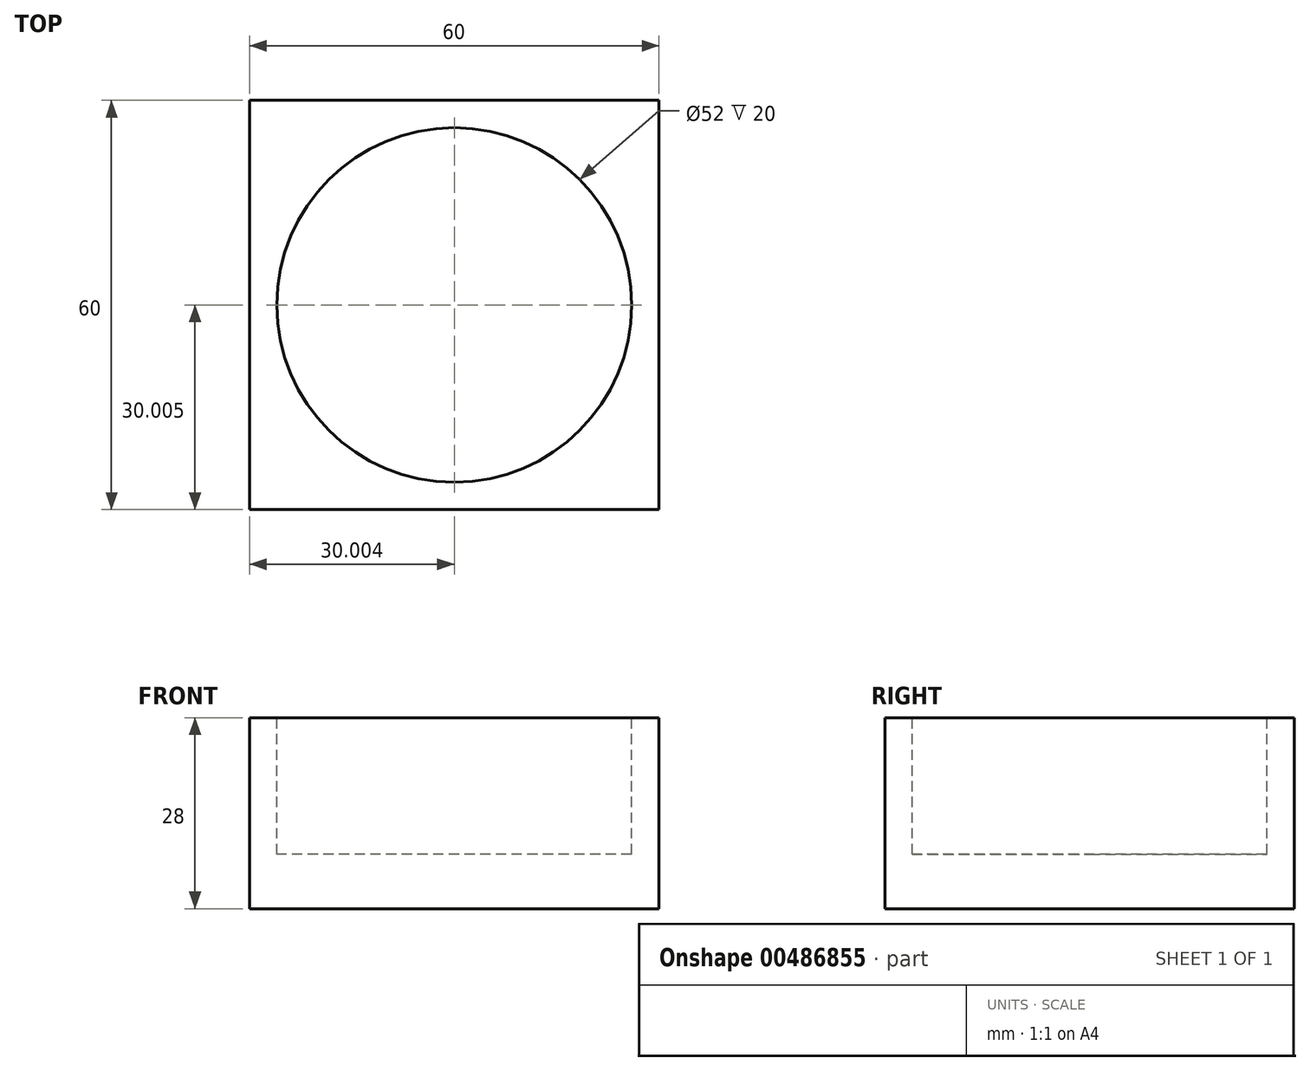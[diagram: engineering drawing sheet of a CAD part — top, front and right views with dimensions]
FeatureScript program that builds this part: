
annotation { "Feature Type Name" : "Feature", "Feature Type Description" : "" }
export const myFeature = defineFeature(function(context is Context, id is Id, definition is map)
    precondition{}
    {
        {
            var Q0;
            Q0=qCreatedBy(makeId("Top.planeOp"),FACE);
            var sketch = newSketch(context, id + "F0", { "sketchPlane" : qUnion([Q0])});
            skLineSegment(sketch, "E0.bottom", {"start": v(-12.17, 33.3) * mm, "end": v(47.83, 33.3) * mm});
            skLineSegment(sketch, "E0.top", {"start": v(-12.17, -26.7) * mm, "end": v(47.83, -26.7) * mm});
            skLineSegment(sketch, "E0.left", {"start": v(-12.17, 33.3) * mm, "end": v(-12.17, -26.7) * mm});
            skLineSegment(sketch, "E0.right", {"start": v(47.83, 33.3) * mm, "end": v(47.83, -26.7) * mm});
            skSolve(sketch);
        }
        {
            var Q0;
            Q0=makeQuery(id+"F0.imprint","IMPRINT",FACE,{"disambiguationData":[TD([[makeQuery(id+"F0.imprint","IMPRINT",EDGE,{"derivedFrom":sQuery(id+"F0.wireOp",EDGE,"E0.bottom")}),-1.0]])]});
            extrude(context, id + "F1", {"entities" : qUnion([Q0]), "depth" : 28 * mm});
        }
        {
            var Q0;
            Q0=makeQuery(id+"F1.opExtrude","CAP_FACE",FACE,{"disambiguationData":[OSD([sQuery(id+"F0.wireOp",EDGE,"E0.bottom"),sQuery(id+"F0.wireOp",EDGE,"E0.top"),sQuery(id+"F0.wireOp",EDGE,"E0.left"),sQuery(id+"F0.wireOp",EDGE,"E0.right")])],"isStart":false});
            var sketch = newSketch(context, id + "F2", { "sketchPlane" : qUnion([Q0])});
            skLineSegment(sketch, "E1", {"start": v(-12.17, 3.3) * mm, "end": v(47.83, 3.3) * mm, "construction": true});
            skLineSegment(sketch, "E2", {"start": v(17.83, 33.3) * mm, "end": v(17.83, -26.7) * mm, "construction": true});
            skCircle(sketch, "E3", {"center": v(17.83, 3.3) * mm, "radius": 26 * mm});
            skSolve(sketch);
        }
        {
            var Q0;
            Q0 = qSketchRegion(id + "F2", true);
            extrude(context, id + "F3", {"entities" : qUnion([Q0]), "operationType" : NewBodyOperationType.REMOVE, "oppositeDirection" : true, "depth" : 20 * mm});
        }
    });
